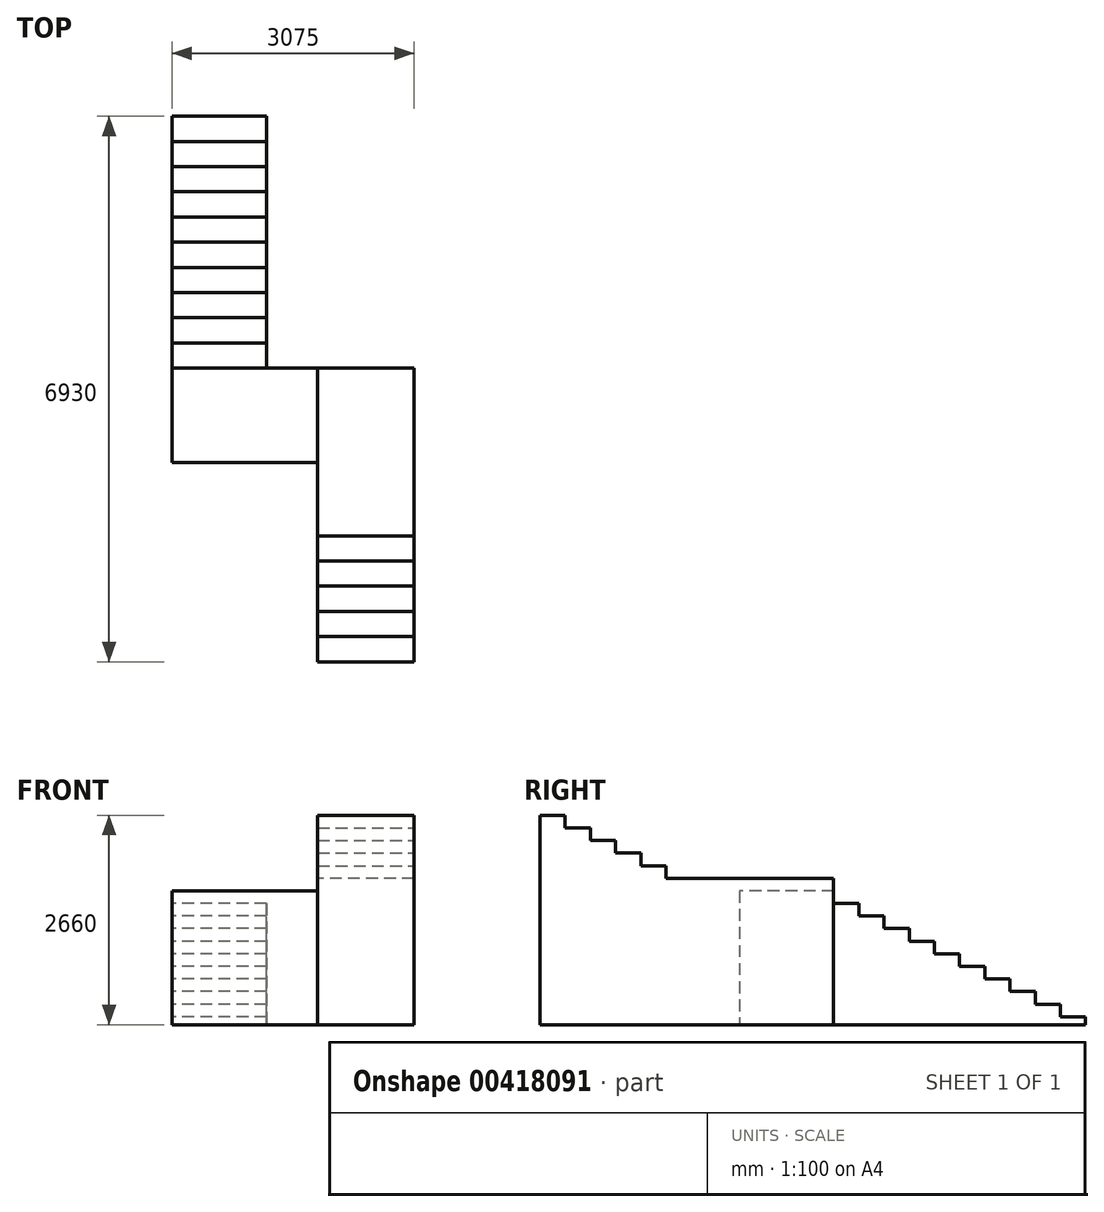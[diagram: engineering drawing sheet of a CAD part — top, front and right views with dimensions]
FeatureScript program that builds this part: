
annotation { "Feature Type Name" : "Feature", "Feature Type Description" : "" }
export const myFeature = defineFeature(function(context is Context, id is Id, definition is map)
    precondition{}
    {
        {
            var Q0;
            Q0=qCreatedBy(makeId("Right.planeOp"),FACE);
            var sketch = newSketch(context, id + "F0", { "sketchPlane" : qUnion([Q0])});
            skLineSegment(sketch, "E0", {"start": v(0, 0) * mm, "end": v(0, 100) * mm});
            skLineSegment(sketch, "E1", {"start": v(0, 100) * mm, "end": v(-320, 100) * mm});
            skLineSegment(sketch, "E2", {"start": v(-320, 100) * mm, "end": v(-320, 260) * mm});
            skLineSegment(sketch, "E3", {"start": v(-320, 260) * mm, "end": v(-640, 260) * mm});
            skLineSegment(sketch, "E4", {"start": v(-640, 260) * mm, "end": v(-640, 420) * mm});
            skLineSegment(sketch, "E5", {"start": v(-640, 420) * mm, "end": v(-960, 420) * mm});
            skLineSegment(sketch, "E6", {"start": v(-960, 420) * mm, "end": v(-960, 580) * mm});
            skLineSegment(sketch, "E7", {"start": v(-960, 580) * mm, "end": v(-1280, 580) * mm});
            skLineSegment(sketch, "E8", {"start": v(-1280, 580) * mm, "end": v(-1280, 740) * mm});
            skLineSegment(sketch, "E9", {"start": v(-1280, 740) * mm, "end": v(-1600, 740) * mm});
            skLineSegment(sketch, "E10", {"start": v(-1600, 740) * mm, "end": v(-1600, 900) * mm});
            skLineSegment(sketch, "E11", {"start": v(-1600, 900) * mm, "end": v(-1920, 900) * mm});
            skLineSegment(sketch, "E12", {"start": v(-1920, 900) * mm, "end": v(-1920, 1060) * mm});
            skLineSegment(sketch, "E13", {"start": v(-1920, 1060) * mm, "end": v(-2240, 1060) * mm});
            skLineSegment(sketch, "E14", {"start": v(-2240, 1060) * mm, "end": v(-2240, 1220) * mm});
            skLineSegment(sketch, "E15", {"start": v(-2240, 1220) * mm, "end": v(-2560, 1220) * mm});
            skLineSegment(sketch, "E16", {"start": v(-2560, 1220) * mm, "end": v(-2560, 1380) * mm});
            skLineSegment(sketch, "E17", {"start": v(-2560, 1380) * mm, "end": v(-2880, 1380) * mm});
            skLineSegment(sketch, "E18", {"start": v(-2880, 1380) * mm, "end": v(-2880, 1540) * mm});
            skLineSegment(sketch, "E19", {"start": v(-2880, 1540) * mm, "end": v(-3200, 1540) * mm});
            skLineSegment(sketch, "E20", {"start": v(-3200, 1540) * mm, "end": v(-3200, 1700) * mm});
            skLineSegment(sketch, "E21", {"start": v(-3200, 1700) * mm, "end": v(-4400, 1700) * mm});
            skLineSegment(sketch, "E22", {"start": v(-4400, 1700) * mm, "end": v(-4400, 0) * mm});
            skLineSegment(sketch, "E23", {"start": v(-4400, 0) * mm, "end": v(0, 0) * mm});
            skSolve(sketch);
        }
        {
            var Q0;
            Q0 = qSketchRegion(id + "F0", true);
            extrude(context, id + "F1", {"entities" : qUnion([Q0]), "depth" : 1200 * mm});
        }
        {
            var Q0;
            Q0=makeQuery(id+"F1.opExtrude","CAP_FACE",FACE,{"disambiguationData":[OSD([sQuery(id+"F0.wireOp",EDGE,"E0"),sQuery(id+"F0.wireOp",EDGE,"E1"),sQuery(id+"F0.wireOp",EDGE,"E2"),sQuery(id+"F0.wireOp",EDGE,"E3"),sQuery(id+"F0.wireOp",EDGE,"E4"),sQuery(id+"F0.wireOp",EDGE,"E5"),sQuery(id+"F0.wireOp",EDGE,"E6"),sQuery(id+"F0.wireOp",EDGE,"E7"),sQuery(id+"F0.wireOp",EDGE,"E8"),sQuery(id+"F0.wireOp",EDGE,"E9"),sQuery(id+"F0.wireOp",EDGE,"E10"),sQuery(id+"F0.wireOp",EDGE,"E11"),sQuery(id+"F0.wireOp",EDGE,"E12"),sQuery(id+"F0.wireOp",EDGE,"E13"),sQuery(id+"F0.wireOp",EDGE,"E14"),sQuery(id+"F0.wireOp",EDGE,"E15"),sQuery(id+"F0.wireOp",EDGE,"E16"),sQuery(id+"F0.wireOp",EDGE,"E17"),sQuery(id+"F0.wireOp",EDGE,"E18"),sQuery(id+"F0.wireOp",EDGE,"E19"),sQuery(id+"F0.wireOp",EDGE,"E20"),sQuery(id+"F0.wireOp",EDGE,"E21"),sQuery(id+"F0.wireOp",EDGE,"E22"),sQuery(id+"F0.wireOp",EDGE,"E23")])],"isStart":false});
            var sketch = newSketch(context, id + "F2", { "sketchPlane" : qUnion([Q0])});
            skLineSegment(sketch, "E24.bottom", {"start": v(-4400, 1700) * mm, "end": v(-3200, 1700) * mm});
            skLineSegment(sketch, "E24.top", {"start": v(-4400, 0) * mm, "end": v(-3200, 0) * mm});
            skLineSegment(sketch, "E24.left", {"start": v(-4400, 1700) * mm, "end": v(-4400, 0) * mm});
            skLineSegment(sketch, "E24.right", {"start": v(-3200, 1700) * mm, "end": v(-3200, 0) * mm});
            skSolve(sketch);
        }
        {
            var Q0;
            {var subQ3=sQuery(id+"F2.wireOp",EDGE,"E24.bottom");Q0=makeQuery(id+"F2.imprint","IMPRINT",FACE,{"disambiguationData":[TD([[makeQuery(id+"F2.imprint","IMPRINT",EDGE,{"derivedFrom":subQ3}),1.0]])]});}
            extrude(context, id + "F3", {"entities" : qUnion([Q0]), "operationType" : NewBodyOperationType.ADD, "depth" : 650 * mm});
        }
        {
            var Q0;
            Q0=makeQuery(id+"F3.opExtrude","CAP_FACE",FACE,{"disambiguationData":[OSD([sQuery(id+"F2.wireOp",EDGE,"E24.bottom"),sQuery(id+"F2.wireOp",EDGE,"E24.top"),sQuery(id+"F2.wireOp",EDGE,"E24.left"),sQuery(id+"F2.wireOp",EDGE,"E24.right")])],"isStart":false});
            var sketch = newSketch(context, id + "F4", { "sketchPlane" : qUnion([Q0])});
            skLineSegment(sketch, "E25.bottom", {"start": v(-3200, 0) * mm, "end": v(-5330, 0) * mm});
            skLineSegment(sketch, "E25.top", {"start": v(-3200, 1860) * mm, "end": v(-5330, 1860) * mm});
            skLineSegment(sketch, "E25.left", {"start": v(-3200, 0) * mm, "end": v(-3200, 1860) * mm});
            skLineSegment(sketch, "E25.right", {"start": v(-5330, 0) * mm, "end": v(-5330, 1860) * mm});
            skSolve(sketch);
        }
        {
            var Q0;
            {var subQ3=sQuery(id+"F4.wireOp",EDGE,"E25.top");Q0=makeQuery(id+"F4.imprint","IMPRINT",FACE,{"disambiguationData":[TD([[makeQuery(id+"F4.imprint","IMPRINT",EDGE,{"derivedFrom":subQ3}),1.0]])]});}
            var Q1;
            {var subQ4=makeQuery(id+"F3.opExtrude","CAP_EDGE",EDGE,{"disambiguationData":[OSD([sQuery(id+"F2.wireOp",EDGE,"E24.bottom")])],"isStart":false});Q1=makeQuery(id+"F4.imprint","IMPRINT",FACE,{"disambiguationData":[TD([[makeQuery(id+"F4.imprint","IMPRINT",EDGE,{"derivedFrom":subQ4}),1.0]])]});}
            extrude(context, id + "F5", {"entities" : qUnion([Q0, Q1]), "operationType" : NewBodyOperationType.ADD, "depth" : 1225 * mm});
        }
        {
            var Q0;
            Q0=makeQuery(id+"F5.opExtrude","CAP_FACE",FACE,{"disambiguationData":[OSD([sQuery(id+"F4.wireOp",EDGE,"E25.bottom"),sQuery(id+"F4.wireOp",EDGE,"E25.top"),sQuery(id+"F4.wireOp",EDGE,"E25.left"),sQuery(id+"F4.wireOp",EDGE,"E25.right")])],"isStart":false});
            var sketch = newSketch(context, id + "F6", { "sketchPlane" : qUnion([Q0])});
            skLineSegment(sketch, "E26", {"start": v(-5330, 0) * mm, "end": v(-5330, 2020) * mm});
            skLineSegment(sketch, "E27", {"start": v(-5330, 2020) * mm, "end": v(-5650, 2020) * mm});
            skLineSegment(sketch, "E28", {"start": v(-5650, 2020) * mm, "end": v(-5650, 2180) * mm});
            skLineSegment(sketch, "E29", {"start": v(-5650, 2180) * mm, "end": v(-5970, 2180) * mm});
            skLineSegment(sketch, "E30", {"start": v(-5970, 2180) * mm, "end": v(-5970, 2340) * mm});
            skLineSegment(sketch, "E31", {"start": v(-5970, 2340) * mm, "end": v(-6290, 2340) * mm});
            skLineSegment(sketch, "E32", {"start": v(-6290, 2340) * mm, "end": v(-6290, 2500) * mm});
            skLineSegment(sketch, "E33", {"start": v(-6290, 2500) * mm, "end": v(-6610, 2500) * mm});
            skLineSegment(sketch, "E34", {"start": v(-6610, 2500) * mm, "end": v(-6610, 2660) * mm});
            skLineSegment(sketch, "E35", {"start": v(-6610, 2660) * mm, "end": v(-6930, 2660) * mm});
            skLineSegment(sketch, "E36", {"start": v(-6930, 2660) * mm, "end": v(-6930, 0) * mm});
            skLineSegment(sketch, "E37", {"start": v(-6930, 0) * mm, "end": v(-5330, 0) * mm});
            skSolve(sketch);
        }
        {
            var Q0;
            {var subQ3=sQuery(id+"F6.wireOp",EDGE,"E27");Q0=makeQuery(id+"F6.imprint","IMPRINT",FACE,{"disambiguationData":[TD([[makeQuery(id+"F6.imprint","IMPRINT",EDGE,{"derivedFrom":subQ3}),1.0]])]});}
            var Q1;
            Q1=makeQuery(id+"F5.opExtrude","CAP_FACE",FACE,{"disambiguationData":[OSD([sQuery(id+"F4.wireOp",EDGE,"E25.bottom"),sQuery(id+"F4.wireOp",EDGE,"E25.top"),sQuery(id+"F4.wireOp",EDGE,"E25.left"),sQuery(id+"F4.wireOp",EDGE,"E25.right")])],"isStart":true});
            extrude(context, id + "F7", {"entities" : qUnion([Q0]), "operationType" : NewBodyOperationType.ADD, "endBound" : BoundingType.UP_TO_SURFACE, "oppositeDirection" : true, "endBoundEntityFace" : qUnion([Q1]), "depth" : 25.4 * mm});
        }
    });
